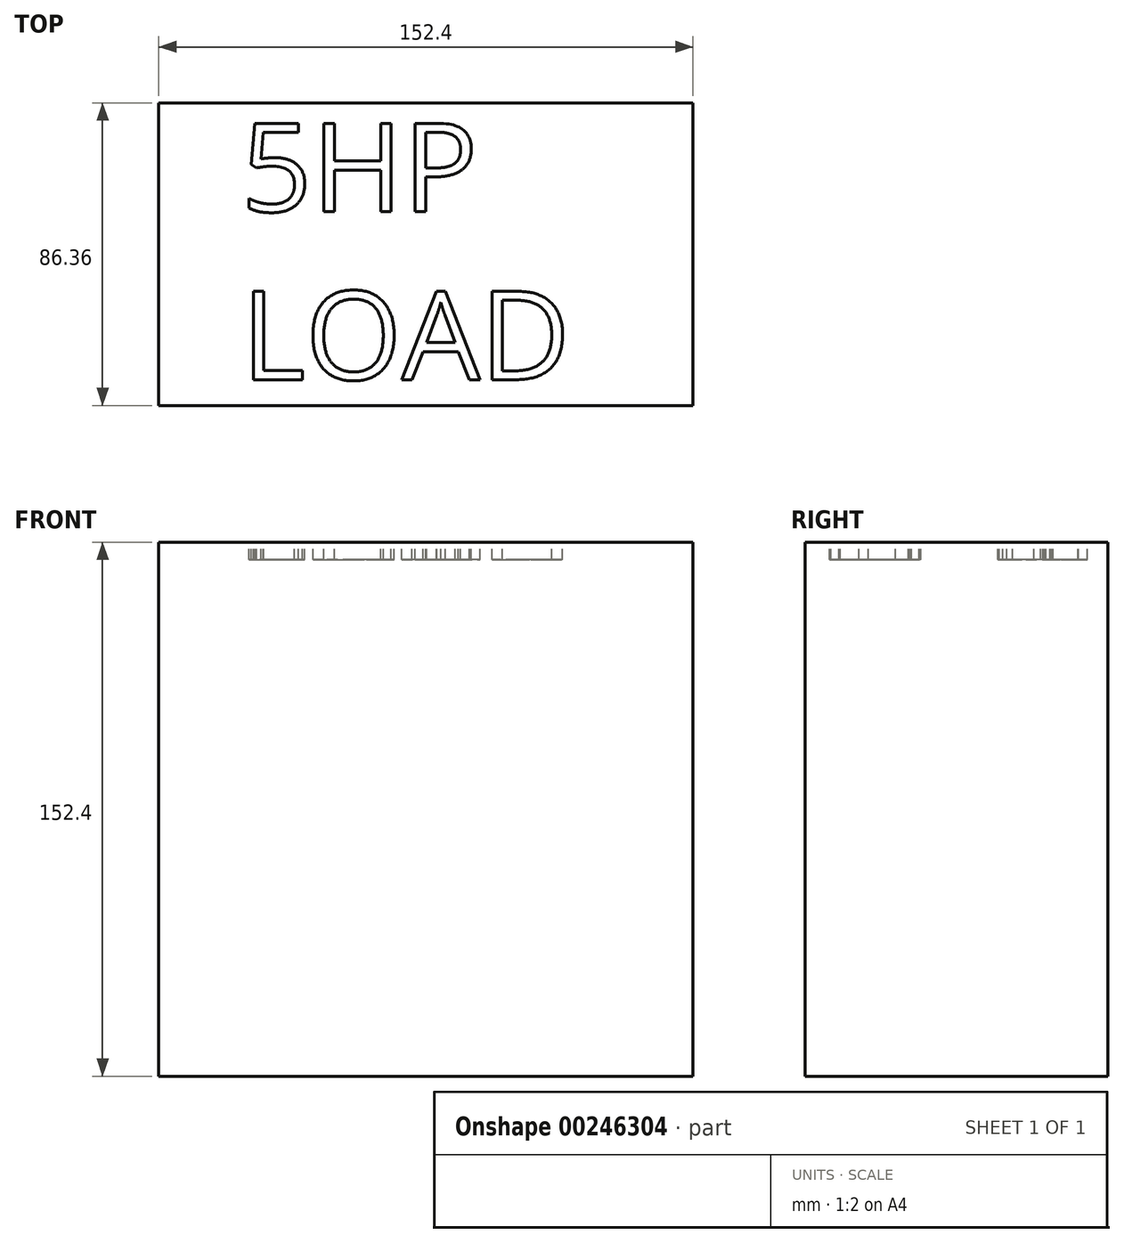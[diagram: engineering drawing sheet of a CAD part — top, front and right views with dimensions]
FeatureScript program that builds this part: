
annotation { "Feature Type Name" : "Feature", "Feature Type Description" : "" }
export const myFeature = defineFeature(function(context is Context, id is Id, definition is map)
    precondition{}
    {
        {
            var Q0;
            Q0=qCreatedBy(makeId("Top.planeOp"),FACE);
            var sketch = newSketch(context, id + "F0", { "sketchPlane" : qUnion([Q0])});
            skLineSegment(sketch, "E0.bottom", {"start": v(-76.2, 43.18) * mm, "end": v(76.2, 43.18) * mm});
            skLineSegment(sketch, "E0.top", {"start": v(-76.2, -43.18) * mm, "end": v(76.2, -43.18) * mm});
            skLineSegment(sketch, "E0.left", {"start": v(-76.2, 43.18) * mm, "end": v(-76.2, -43.18) * mm});
            skLineSegment(sketch, "E0.right", {"start": v(76.2, 43.18) * mm, "end": v(76.2, -43.18) * mm});
            skPoint(sketch, "E0.middle", {"position": v(0, 0) * mm});
            skSolve(sketch);
        }
        {
            var Q0;
            Q0=makeQuery(id+"F0.imprint","IMPRINT",FACE,{"disambiguationData":[TD([[makeQuery(id+"F0.imprint","IMPRINT",EDGE,{"derivedFrom":sQuery(id+"F0.wireOp",EDGE,"E0.bottom")}),-1.0]])]});
            extrude(context, id + "F1", {"entities" : qUnion([Q0]), "depth" : 152.4 * mm});
        }
        {
            var Q0;
            Q0=makeQuery(id+"F1.opExtrude","CAP_FACE",FACE,{"disambiguationData":[OSD([sQuery(id+"F0.wireOp",EDGE,"E0.bottom"),sQuery(id+"F0.wireOp",EDGE,"E0.top"),sQuery(id+"F0.wireOp",EDGE,"E0.left"),sQuery(id+"F0.wireOp",EDGE,"E0.right")])],"isStart":false});
            var sketch = newSketch(context, id + "F2", { "sketchPlane" : qUnion([Q0])});
            skText(sketch, "E1", { "text": "5HP\nLOAD", "fontName": "OpenSans-Regular.ttf"});
            const initialGuessF2  = {"E1": [-0.05268, 0.01215, 1, 0, 0.0254]};
            skSetInitialGuess(sketch, initialGuessF2);
            skSolve(sketch);
        }
        {
            var Q0;
            Q0 = qSketchRegion(id + "F2", true);
            extrude(context, id + "F3", {"entities" : qUnion([Q0]), "operationType" : NewBodyOperationType.REMOVE, "oppositeDirection" : true, "depth" : 5 * mm});
        }
    });
